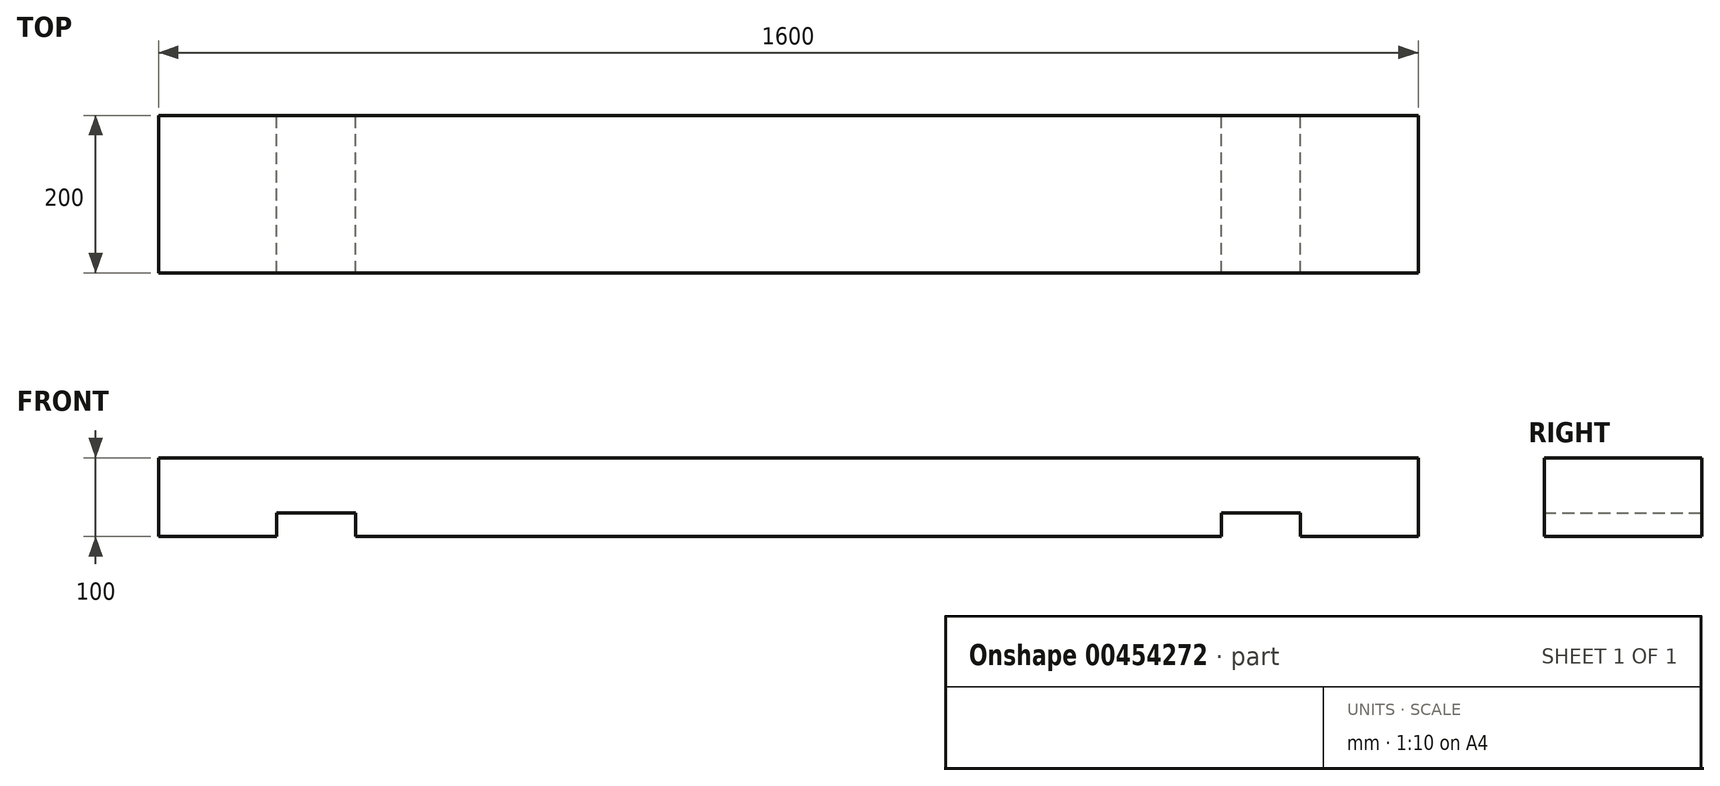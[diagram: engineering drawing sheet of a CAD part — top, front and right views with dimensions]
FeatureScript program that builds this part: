
annotation { "Feature Type Name" : "Feature", "Feature Type Description" : "" }
export const myFeature = defineFeature(function(context is Context, id is Id, definition is map)
    precondition{}
    {
        {
            var Q0;
            Q0=qCreatedBy(makeId("Front.planeOp"),FACE);
            var sketch = newSketch(context, id + "F0", { "sketchPlane" : qUnion([Q0])});
            skLineSegment(sketch, "E0.bottom", {"start": v(800, 50) * mm, "end": v(-800, 50) * mm});
            skLineSegment(sketch, "E0.top", {"start": v(800, -50) * mm, "end": v(650, -50) * mm});
            skLineSegment(sketch, "E0.left", {"start": v(800, 50) * mm, "end": v(800, -50) * mm});
            skLineSegment(sketch, "E0.right", {"start": v(-800, 50) * mm, "end": v(-800, -50) * mm});
            skPoint(sketch, "E0.middle", {"position": v(0, 0) * mm});
            skLineSegment(sketch, "E1", {"start": v(-650, -50) * mm, "end": v(-650, -20) * mm});
            skLineSegment(sketch, "E2", {"start": v(-650, -20) * mm, "end": v(-550, -20) * mm});
            skLineSegment(sketch, "E3", {"start": v(-550, -20) * mm, "end": v(-550, -50) * mm});
            skLineSegment(sketch, "E4.trimOffspring", {"start": v(-650, -50) * mm, "end": v(-800, -50) * mm});
            skLineSegment(sketch, "E5", {"start": v(0, 50) * mm, "end": v(0, -50) * mm, "construction": true});
            skLineSegment(sketch, "E6", {"start": v(550, -50) * mm, "end": v(550, -20) * mm});
            skLineSegment(sketch, "E7", {"start": v(550, -20) * mm, "end": v(650, -20) * mm});
            skLineSegment(sketch, "E8", {"start": v(650, -20) * mm, "end": v(650, -50) * mm});
            skLineSegment(sketch, "E9.trimOffspring", {"start": v(550, -50) * mm, "end": v(-550, -50) * mm});
            skSolve(sketch);
        }
        {
            var Q0;
            Q0 = qSketchRegion(id + "F0", true);
            extrude(context, id + "F1", {"entities" : qUnion([Q0]), "depth" : 200 * mm});
        }
    });
